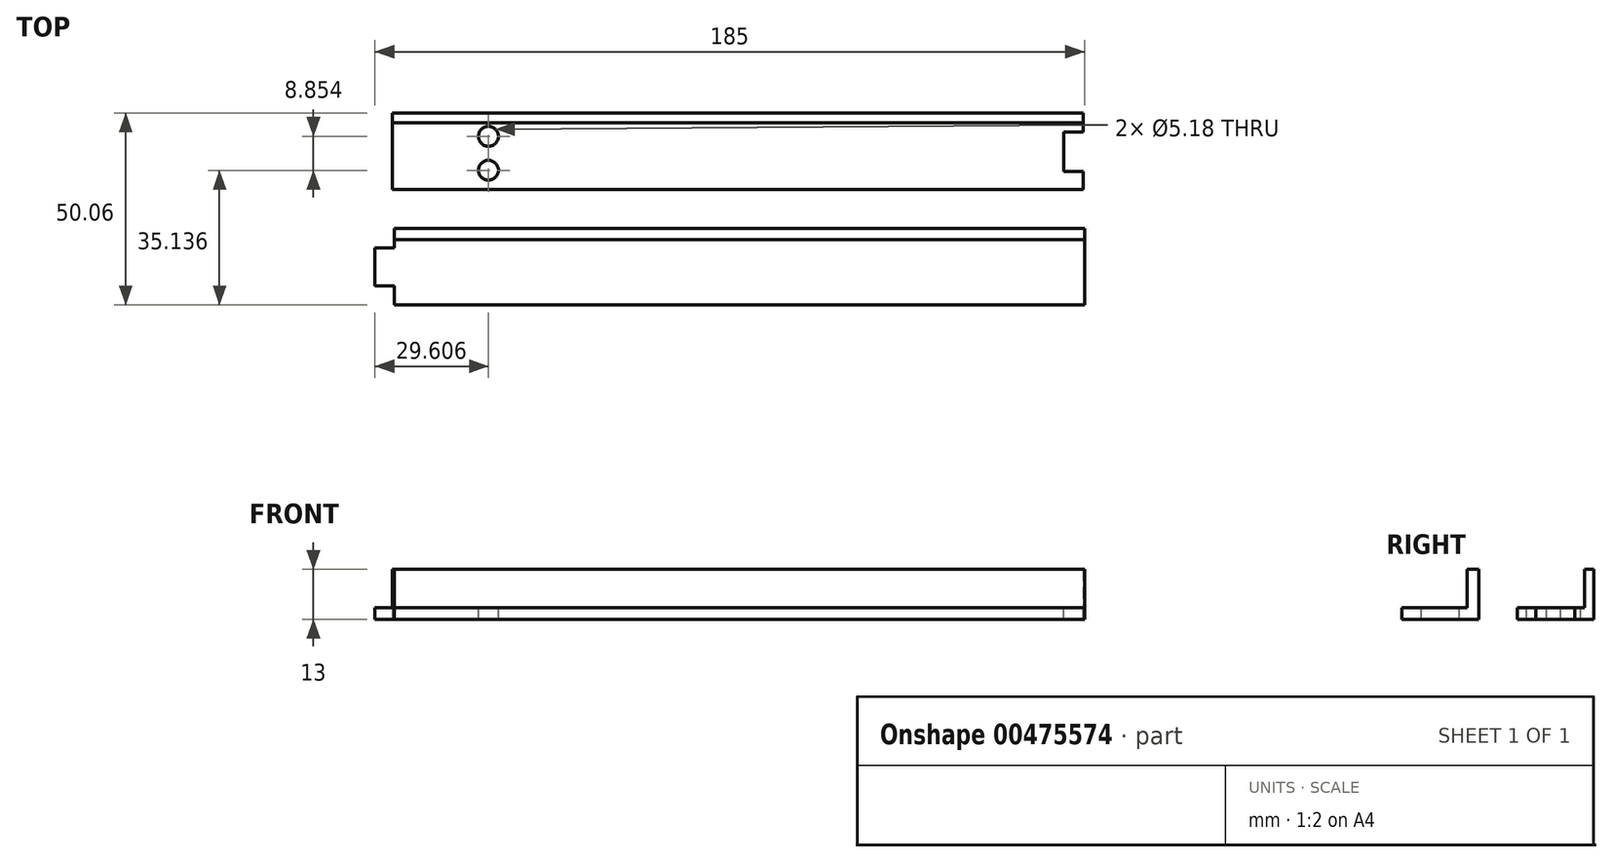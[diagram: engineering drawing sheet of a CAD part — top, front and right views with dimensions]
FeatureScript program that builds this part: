
annotation { "Feature Type Name" : "Feature", "Feature Type Description" : "" }
export const myFeature = defineFeature(function(context is Context, id is Id, definition is map)
    precondition{}
    {
        {
            var Q0;
            Q0=qCreatedBy(makeId("Top.planeOp"),FACE);
            var sketch = newSketch(context, id + "F0", { "sketchPlane" : qUnion([Q0])});
            skLineSegment(sketch, "E0.bottom", {"start": v(-91.1, 27.92) * mm, "end": v(88.9, 27.92) * mm});
            skLineSegment(sketch, "E0.top", {"start": v(-91.1, 7.92) * mm, "end": v(88.9, 7.92) * mm});
            skLineSegment(sketch, "E0.left", {"start": v(-91.1, 27.92) * mm, "end": v(-91.1, 7.92) * mm});
            skLineSegment(sketch, "E0.right", {"start": v(88.9, 27.92) * mm, "end": v(88.9, 7.92) * mm});
            skLineSegment(sketch, "E1.bottom", {"start": v(-90.7, -2.14) * mm, "end": v(89.3, -2.14) * mm});
            skLineSegment(sketch, "E1.top", {"start": v(-90.7, -22.14) * mm, "end": v(89.3, -22.14) * mm});
            skLineSegment(sketch, "E1.left", {"start": v(-90.7, -2.14) * mm, "end": v(-90.7, -22.14) * mm});
            skLineSegment(sketch, "E1.right", {"start": v(89.3, -2.14) * mm, "end": v(89.3, -22.14) * mm});
            skLineSegment(sketch, "E2.bottom", {"start": v(-90.7, -7.24) * mm, "end": v(-95.7, -7.24) * mm});
            skLineSegment(sketch, "E2.top", {"start": v(-90.7, -17.14) * mm, "end": v(-95.7, -17.14) * mm});
            skLineSegment(sketch, "E2.left", {"start": v(-90.7, -7.24) * mm, "end": v(-90.7, -17.14) * mm});
            skLineSegment(sketch, "E2.right", {"start": v(-95.7, -7.24) * mm, "end": v(-95.7, -17.14) * mm});
            skSolve(sketch);
        }
        {
            var Q0;
            Q0 = qSketchRegion(id + "F0", true);
            extrude(context, id + "F1", {"entities" : qUnion([Q0]), "depth" : 3 * mm, "offsetDistance" : 25 * mm});
        }
        {
            var Q0;
            Q0=makeQuery(id+"F1.opExtrude","CAP_FACE",FACE,{"disambiguationData":[OSD([sQuery(id+"F0.wireOp",EDGE,"E0.bottom"),sQuery(id+"F0.wireOp",EDGE,"E0.top"),sQuery(id+"F0.wireOp",EDGE,"E0.left"),sQuery(id+"F0.wireOp",EDGE,"E0.right")])],"isStart":false});
            var sketch = newSketch(context, id + "F2", { "sketchPlane" : qUnion([Q0])});
            skLineSegment(sketch, "E3.bottom", {"start": v(88.9, 22.92) * mm, "end": v(83.9, 22.92) * mm});
            skLineSegment(sketch, "E3.top", {"start": v(88.9, 12.72) * mm, "end": v(83.9, 12.72) * mm});
            skLineSegment(sketch, "E3.left", {"start": v(88.9, 22.92) * mm, "end": v(88.9, 12.72) * mm});
            skLineSegment(sketch, "E3.right", {"start": v(83.9, 22.92) * mm, "end": v(83.9, 12.72) * mm});
            skSolve(sketch);
        }
        {
            var Q0;
            Q0 = qSketchRegion(id + "F2", true);
            extrude(context, id + "F3", {"entities" : qUnion([Q0]), "operationType" : NewBodyOperationType.REMOVE, "oppositeDirection" : true, "depth" : 3 * mm, "offsetDistance" : 25 * mm});
        }
        {
            var Q0;
            Q0=makeQuery(id+"F1.opExtrude","CAP_FACE",FACE,{"disambiguationData":[OSD([sQuery(id+"F0.wireOp",EDGE,"E0.bottom"),sQuery(id+"F0.wireOp",EDGE,"E0.top"),sQuery(id+"F0.wireOp",EDGE,"E0.left"),sQuery(id+"F0.wireOp",EDGE,"E0.right")])],"isStart":false});
            var sketch = newSketch(context, id + "F4", { "sketchPlane" : qUnion([Q0])});
            skLineSegment(sketch, "E4.bottom", {"start": v(-91.1, 27.92) * mm, "end": v(88.9, 27.92) * mm});
            skLineSegment(sketch, "E4.top", {"start": v(-91.1, 25.42) * mm, "end": v(88.9, 25.42) * mm});
            skLineSegment(sketch, "E4.left", {"start": v(-91.1, 27.92) * mm, "end": v(-91.1, 25.42) * mm});
            skLineSegment(sketch, "E4.right", {"start": v(88.9, 27.92) * mm, "end": v(88.9, 25.42) * mm});
            skSolve(sketch);
        }
        {
            var Q0;
            Q0 = qSketchRegion(id + "F4", true);
            extrude(context, id + "F5", {"entities" : qUnion([Q0]), "operationType" : NewBodyOperationType.ADD, "depth" : 10 * mm, "offsetDistance" : 25 * mm});
        }
        {
            var Q0;
            Q0=makeQuery(id+"F1.opExtrude","CAP_FACE",FACE,{"disambiguationData":[OSD([sQuery(id+"F0.wireOp",EDGE,"E1.bottom"),sQuery(id+"F0.wireOp",EDGE,"E1.top"),sQuery(id+"F0.wireOp",EDGE,"E1.left"),sQuery(id+"F0.wireOp",EDGE,"E1.right")])],"isStart":false});
            var sketch = newSketch(context, id + "F6", { "sketchPlane" : qUnion([Q0])});
            skLineSegment(sketch, "E5.bottom", {"start": v(-90.7, -2.14) * mm, "end": v(89.3, -2.14) * mm});
            skLineSegment(sketch, "E5.top", {"start": v(-90.7, -5.14) * mm, "end": v(89.3, -5.14) * mm});
            skLineSegment(sketch, "E5.left", {"start": v(-90.7, -2.14) * mm, "end": v(-90.7, -5.14) * mm});
            skLineSegment(sketch, "E5.right", {"start": v(89.3, -2.14) * mm, "end": v(89.3, -5.14) * mm});
            skSolve(sketch);
        }
        {
            var Q0;
            Q0 = qSketchRegion(id + "F6", true);
            extrude(context, id + "F7", {"entities" : qUnion([Q0]), "operationType" : NewBodyOperationType.ADD, "depth" : 10 * mm, "offsetDistance" : 25 * mm});
        }
        {
            var Q0;
            Q0=makeQuery(id+"F1.opExtrude","CAP_FACE",FACE,{"disambiguationData":[OSD([sQuery(id+"F0.wireOp",EDGE,"E0.bottom"),sQuery(id+"F0.wireOp",EDGE,"E0.top"),sQuery(id+"F0.wireOp",EDGE,"E0.left"),sQuery(id+"F0.wireOp",EDGE,"E0.right")])],"isStart":false});
            var sketch = newSketch(context, id + "F8", { "sketchPlane" : qUnion([Q0])});
            skCircle(sketch, "E6", {"center": v(-66.1, 21.85) * mm, "radius": 2.6 * mm});
            skCircle(sketch, "E7", {"center": v(-66.1, 13) * mm, "radius": 2.6 * mm});
            skSolve(sketch);
        }
        {
            var Q0;
            Q0 = qSketchRegion(id + "F8", true);
            extrude(context, id + "F9", {"entities" : qUnion([Q0]), "operationType" : NewBodyOperationType.REMOVE, "oppositeDirection" : true, "depth" : 3 * mm, "offsetDistance" : 25 * mm});
        }
    });
